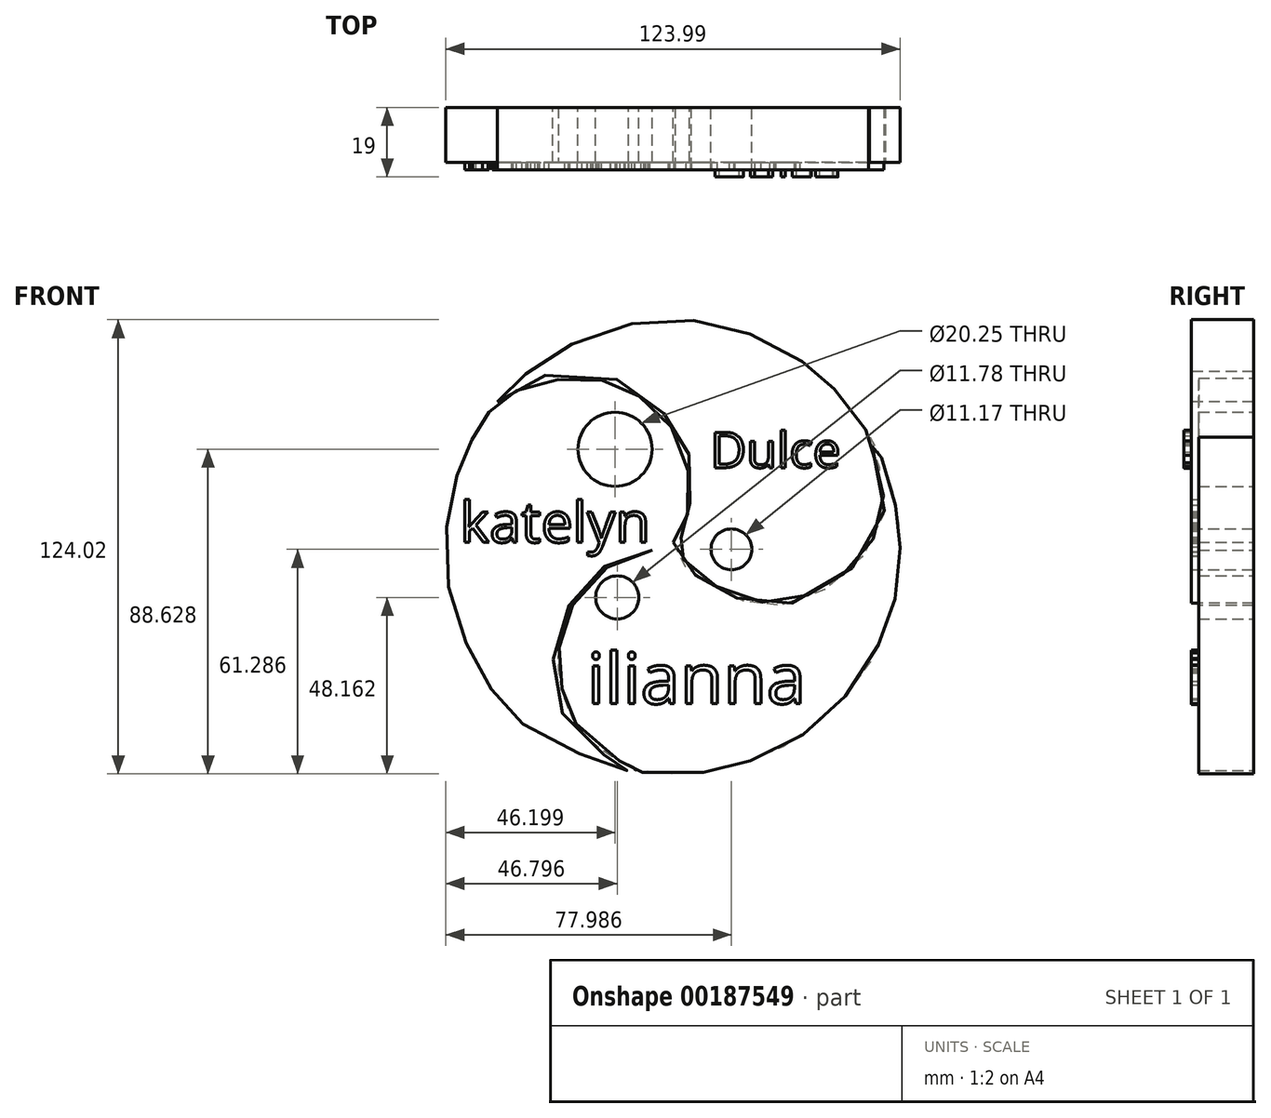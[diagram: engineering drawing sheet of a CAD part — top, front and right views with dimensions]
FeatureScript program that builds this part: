
annotation { "Feature Type Name" : "Feature", "Feature Type Description" : "" }
export const myFeature = defineFeature(function(context is Context, id is Id, definition is map)
    precondition{}
    {
        {
            var Q0;
            Q0=qCreatedBy(makeId("Front.planeOp"),FACE);
            var sketch = newSketch(context, id + "F0", { "sketchPlane" : qUnion([Q0])});
            skFitSpline(sketch, "E0", {"points": [v(0, 0) * mm, v(3.96, 7.77) * mm, v(2.74, 25.44) * mm, v(-8.53, 39.45) * mm, v(-21.63, 44.63) * mm, v(-39.3, 42.8) * mm, v(-49.35, 36.71) * mm, v(-54.53, 28.8) * mm, v(-59.7, 16) * mm, v(-61.23, -12.34) * mm, v(-50.88, -38.24) * mm, v(-35.34, -53.16) * mm, v(-12.19, -62.3) * mm, v(-26.5, -51.95) * mm, v(-31.99, -26.96) * mm, v(-18.28, -6.25) * mm, v(0, 0) * mm]});
            skFitSpline(sketch, "E1", {"points": [v(0, 0) * mm, v(2.56, -5.68) * mm, v(10.55, -11.53) * mm, v(20.12, -16.22) * mm, v(35.3, -15.8) * mm, v(53.48, -1.53) * mm, v(57.46, 16.11) * mm, v(53.64, 28.69) * mm, v(54.66, 27.84) * mm, v(59.37, 15.9) * mm, v(61.05, 8.2) * mm, v(61.91, 0) * mm, v(61.13, -12.63) * mm, v(58.57, -21.74) * mm, v(52.22, -35.22) * mm, v(41.13, -47.88) * mm, v(29.75, -55.97) * mm, v(15.23, -61.48) * mm, v(5.63, -62.99) * mm, v(-9.85, -62.43) * mm, v(-10.74, -61.61) * mm, v(-11.71, -61.07) * mm, v(-22.38, -54.48) * mm, v(-28.7, -45.14) * mm, v(-30.18, -40.34) * mm, v(-31.3, -33.08) * mm, v(-30.3, -24.47) * mm, v(-26.39, -15.53) * mm, v(-18.06, -6.87) * mm, v(-12.82, -4.8) * mm, v(-0.05, 0.07) * mm, v(0, 0) * mm]});
            skFitSpline(sketch, "E2", {"points": [v(-48, 38.36) * mm, v(-47.75, 38.91) * mm, v(-40.33, 45.88) * mm, v(-28.96, 53.47) * mm, v(-11.87, 59.64) * mm, v(5.77, 60.58) * mm, v(20.8, 57.03) * mm, v(34.96, 49.53) * mm, v(41.03, 44.87) * mm, v(48.72, 36.33) * mm, v(53.36, 29.1) * mm, v(53.15, 28) * mm, v(56.03, 20.38) * mm, v(57.32, 14.6) * mm, v(57.06, 6.52) * mm, v(52.2, -2.58) * mm, v(46.16, -8.95) * mm, v(39.28, -13.3) * mm, v(29.09, -16.41) * mm, v(21.14, -15.66) * mm, v(10.5, -11.3) * mm, v(4.53, -6.69) * mm, v(0.56, -0.3) * mm, v(1.38, 0.37) * mm, v(2.42, 1.62) * mm, v(3.87, 4.94) * mm, v(4.76, 15.87) * mm, v(3.92, 25.5) * mm, v(-2.03, 34.75) * mm, v(-13.93, 43.94) * mm, v(-37.1, 44.92) * mm, v(-48, 38.36) * mm]});
            skSolve(sketch);
        }
        {
            var Q0;
            Q0 = qSketchRegion(id + "F0", true);
            extrude(context, id + "F1", {"entities" : qUnion([Q0]), "depth" : 15 * mm});
        }
        {
            var Q0;
            Q0=qCreatedBy(makeId("Front.planeOp"),FACE);
            var sketch = newSketch(context, id + "F2", { "sketchPlane" : qUnion([Q0])});
            skCircle(sketch, "E3", {"center": v(-15.84, 25.44) * mm, "radius": 10.13 * mm});
            skSolve(sketch);
        }
        {
            var Q0;
            Q0 = qSketchRegion(id + "F2", true);
            extrude(context, id + "F3", {"entities" : qUnion([Q0]), "operationType" : NewBodyOperationType.REMOVE, "depth" : 25 * mm});
        }
        {
            var Q0;
            Q0=qCreatedBy(makeId("Front.planeOp"),FACE);
            var sketch = newSketch(context, id + "F4", { "sketchPlane" : qUnion([Q0])});
            skText(sketch, "E4", { "text": "katelyn", "fontName": "OpenSans-Regular.ttf"});
            const initialGuessF4  = {"E4": [-0.05822, 0, 1, 0, 0.01112]};
            skSetInitialGuess(sketch, initialGuessF4);
            skSolve(sketch);
        }
        {
            var Q0;
            Q0 = qSketchRegion(id + "F4", true);
            extrude(context, id + "F5", {"entities" : qUnion([Q0]), "operationType" : NewBodyOperationType.ADD, "depth" : 17 * mm});
        }
        {
            var Q0;
            Q0=makeQuery(id+"F1.opExtrude","CAP_FACE",FACE,{"disambiguationData":[OSD([sQuery(id+"F0.wireOp",EDGE,"E2")])],"isStart":false});
            extrude(context, id + "F6", {"entities" : qUnion([Q0]), "operationType" : NewBodyOperationType.ADD, "depth" : 2 * mm});
        }
        {
            var Q0;
            Q0=qCreatedBy(makeId("Front.planeOp"),FACE);
            var sketch = newSketch(context, id + "F7", { "sketchPlane" : qUnion([Q0])});
            skCircle(sketch, "E5", {"center": v(-15.24, -15.03) * mm, "radius": 5.89 * mm});
            skSolve(sketch);
        }
        {
            var Q0;
            Q0 = qSketchRegion(id + "F7", true);
            extrude(context, id + "F8", {"entities" : qUnion([Q0]), "operationType" : NewBodyOperationType.REMOVE, "depth" : 26 * mm});
        }
        {
            var Q0;
            Q0=qCreatedBy(makeId("Front.planeOp"),FACE);
            var sketch = newSketch(context, id + "F9", { "sketchPlane" : qUnion([Q0])});
            skText(sketch, "E6", { "text": "ilianna", "fontName": "OpenSans-Regular.ttf"});
            const initialGuessF9  = {"E6": [-0.02349, -0.04405, 1, 0, 0.01388]};
            skSetInitialGuess(sketch, initialGuessF9);
            skSolve(sketch);
        }
        {
            var Q0;
            Q0 = qSketchRegion(id + "F9", true);
            extrude(context, id + "F10", {"entities" : qUnion([Q0]), "operationType" : NewBodyOperationType.ADD, "depth" : 17 * mm});
        }
        {
            var Q0;
            Q0=qCreatedBy(makeId("Front.planeOp"),FACE);
            var sketch = newSketch(context, id + "F11", { "sketchPlane" : qUnion([Q0])});
            skCircle(sketch, "E7", {"center": v(15.95, -1.9) * mm, "radius": 5.59 * mm});
            skSolve(sketch);
        }
        {
            var Q0;
            Q0 = qSketchRegion(id + "F11", true);
            extrude(context, id + "F12", {"entities" : qUnion([Q0]), "operationType" : NewBodyOperationType.REMOVE, "depth" : 26 * mm});
        }
        {
            var Q0;
            Q0=qCreatedBy(makeId("Front.planeOp"),FACE);
            var sketch = newSketch(context, id + "F13", { "sketchPlane" : qUnion([Q0])});
            skText(sketch, "E8", { "text": "Dulce", "fontName": "OpenSans-Regular.ttf"});
            const initialGuessF13  = {"E8": [0.01017, 0.02042, 1, 0, 0.00973]};
            skSetInitialGuess(sketch, initialGuessF13);
            skSolve(sketch);
        }
        {
            var Q0;
            Q0 = qSketchRegion(id + "F13", true);
            extrude(context, id + "F14", {"entities" : qUnion([Q0]), "operationType" : NewBodyOperationType.ADD, "depth" : 19 * mm});
        }
    });
